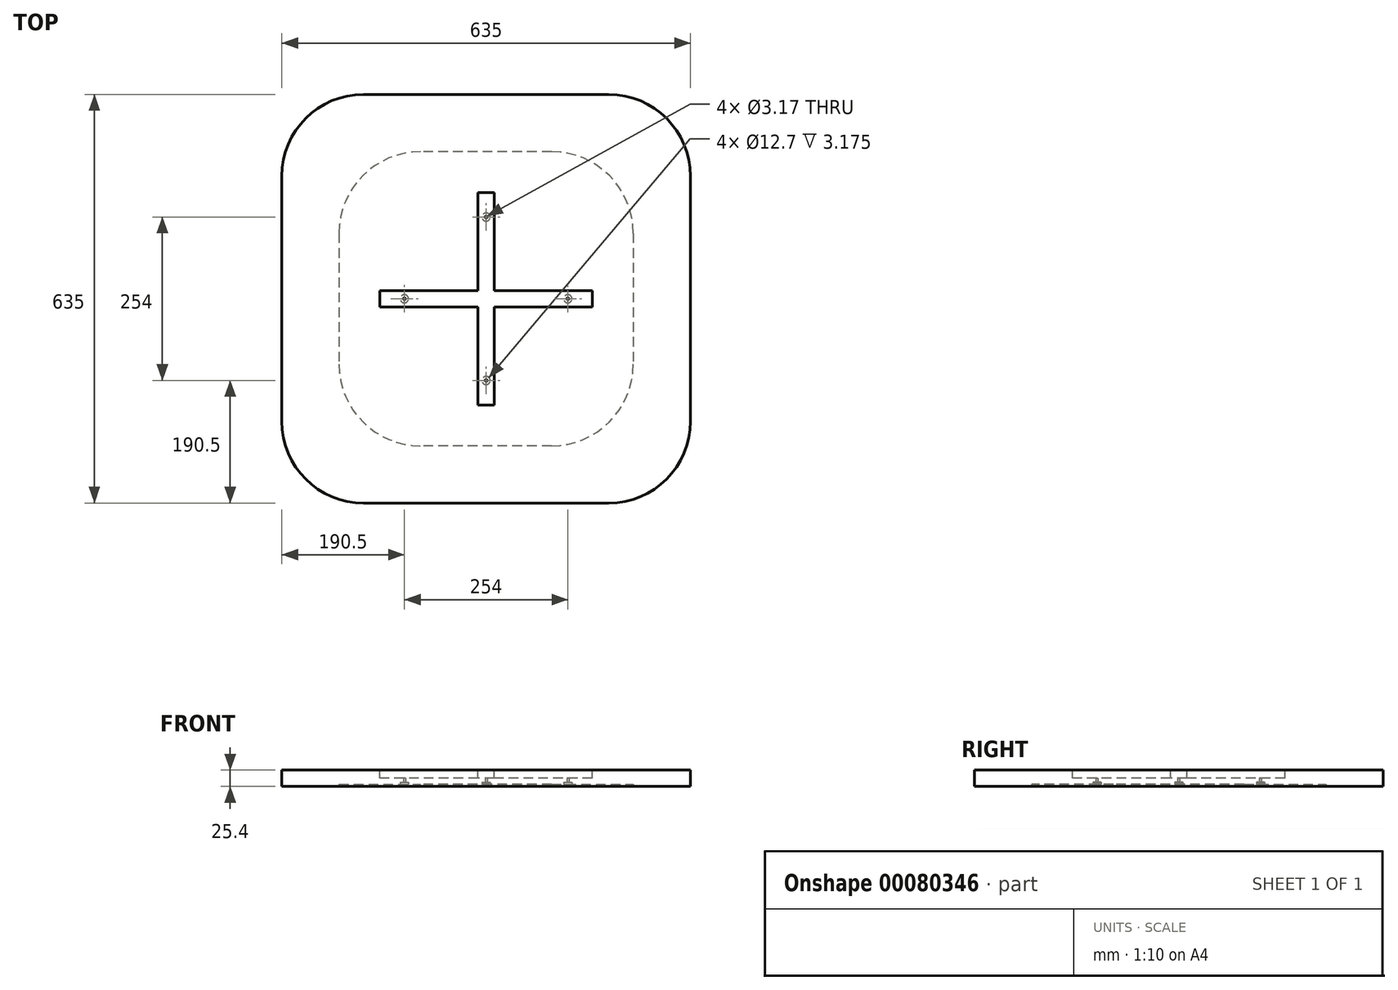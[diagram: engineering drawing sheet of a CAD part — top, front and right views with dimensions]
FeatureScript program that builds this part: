
annotation { "Feature Type Name" : "Feature", "Feature Type Description" : "" }
export const myFeature = defineFeature(function(context is Context, id is Id, definition is map)
    precondition{}
    {
        {
            var Q0;
            Q0=qCreatedBy(makeId("Top.planeOp"),FACE);
            var sketch = newSketch(context, id + "F0", { "sketchPlane" : qUnion([Q0])});
            skLineSegment(sketch, "E0.bottom", {"start": v(317.5, 317.5) * mm, "end": v(-317.5, 317.5) * mm});
            skLineSegment(sketch, "E0.top", {"start": v(317.5, -317.5) * mm, "end": v(-317.5, -317.5) * mm});
            skLineSegment(sketch, "E0.left", {"start": v(317.5, 317.5) * mm, "end": v(317.5, -317.5) * mm});
            skLineSegment(sketch, "E0.right", {"start": v(-317.5, 317.5) * mm, "end": v(-317.5, -317.5) * mm});
            skPoint(sketch, "E0.middle", {"position": v(0, 0) * mm});
            skSolve(sketch);
        }
        {
            var Q0;
            Q0=makeQuery(id+"F0.imprint","IMPRINT",FACE,{"disambiguationData":[TD([[makeQuery(id+"F0.imprint","IMPRINT",EDGE,{"derivedFrom":sQuery(id+"F0.wireOp",EDGE,"E0.bottom")}),1.0]])]});
            extrude(context, id + "F1", {"entities" : qUnion([Q0]), "depth" : 25.4 * mm});
        }
        {
            var Q0;
            Q0=makeQuery(id+"F1.opExtrude","CAP_FACE",FACE,{"disambiguationData":[OSD([sQuery(id+"F0.wireOp",EDGE,"E0.bottom"),sQuery(id+"F0.wireOp",EDGE,"E0.top"),sQuery(id+"F0.wireOp",EDGE,"E0.left"),sQuery(id+"F0.wireOp",EDGE,"E0.right")])],"isStart":false});
            var sketch = newSketch(context, id + "F8", { "sketchPlane" : qUnion([Q0])});
            skLineSegment(sketch, "E1.bottom", {"start": v(12.7, 165.1) * mm, "end": v(-12.7, 165.1) * mm});
            skLineSegment(sketch, "E1.top", {"start": v(12.7, -165.1) * mm, "end": v(-12.7, -165.1) * mm});
            skLineSegment(sketch, "E1.left", {"start": v(12.7, 165.1) * mm, "end": v(12.7, 12.7) * mm});
            skLineSegment(sketch, "E1.right", {"start": v(-12.7, 165.1) * mm, "end": v(-12.7, 12.7) * mm});
            skPoint(sketch, "E1.middle", {"position": v(0, 0) * mm});
            skLineSegment(sketch, "E2.bottom", {"start": v(165.1, 12.7) * mm, "end": v(12.7, 12.7) * mm});
            skLineSegment(sketch, "E2.top", {"start": v(165.1, -12.7) * mm, "end": v(12.7, -12.7) * mm});
            skLineSegment(sketch, "E2.left", {"start": v(165.1, 12.7) * mm, "end": v(165.1, -12.7) * mm});
            skLineSegment(sketch, "E2.right", {"start": v(-165.1, 12.7) * mm, "end": v(-165.1, -12.7) * mm});
            skLineSegment(sketch, "E3.trimOffspring", {"start": v(12.7, -12.7) * mm, "end": v(12.7, -165.1) * mm});
            skLineSegment(sketch, "E4.trimOffspring", {"start": v(-12.7, 12.7) * mm, "end": v(-165.1, 12.7) * mm});
            skLineSegment(sketch, "E5.trimOffspring", {"start": v(-12.7, -12.7) * mm, "end": v(-12.7, -165.1) * mm});
            skLineSegment(sketch, "E6.trimOffspring", {"start": v(-12.7, -12.7) * mm, "end": v(-165.1, -12.7) * mm});
            skSolve(sketch);
        }
        {
            var Q0;
            Q0=qSketchRegion(id+"F8",true);
            extrude(context, id + "F9", {"entities" : qUnion([Q0]), "operationType" : NewBodyOperationType.REMOVE, "oppositeDirection" : true, "depth" : 12.7 * mm});
        }
        {
            var Q0;
            Q0=makeQuery(id+"F1.opExtrude","SWEPT_EDGE",EDGE,{"disambiguationData":[OSD([sQuery(id+"F0.wireOp",EDGE,"E0.top"),sQuery(id+"F0.wireOp",EDGE,"E0.right")])]});
            var Q1;
            Q1=makeQuery(id+"F1.opExtrude","SWEPT_EDGE",EDGE,{"disambiguationData":[OSD([sQuery(id+"F0.wireOp",EDGE,"E0.top"),sQuery(id+"F0.wireOp",EDGE,"E0.left")])]});
            var Q2;
            Q2=makeQuery(id+"F1.opExtrude","SWEPT_EDGE",EDGE,{"disambiguationData":[OSD([sQuery(id+"F0.wireOp",EDGE,"E0.bottom"),sQuery(id+"F0.wireOp",EDGE,"E0.left")])]});
            var Q3;
            Q3=makeQuery(id+"F1.opExtrude","SWEPT_EDGE",EDGE,{"disambiguationData":[OSD([sQuery(id+"F0.wireOp",EDGE,"E0.bottom"),sQuery(id+"F0.wireOp",EDGE,"E0.right")])]});
            fillet(context, id + "F2", {"entities" : qUnion([Q0, Q1, Q2, Q3]), "radius" : 127 * mm, "tangentPropagation" : true, "allowEdgeOverflow" : false});
        }
        {
            var Q0;
            Q0=makeQuery(id+"F1.opExtrude","CAP_FACE",FACE,{"disambiguationData":[OSD([sQuery(id+"F0.wireOp",EDGE,"E0.bottom"),sQuery(id+"F0.wireOp",EDGE,"E0.top"),sQuery(id+"F0.wireOp",EDGE,"E0.left"),sQuery(id+"F0.wireOp",EDGE,"E0.right")])],"isStart":true});
            var sketch = newSketch(context, id + "F3", { "sketchPlane" : qUnion([Q0])});
            skLineSegment(sketch, "E7.bottom", {"start": v(228.6, -228.6) * mm, "end": v(-228.6, -228.6) * mm});
            skLineSegment(sketch, "E7.top", {"start": v(228.6, 228.6) * mm, "end": v(-228.6, 228.6) * mm});
            skLineSegment(sketch, "E7.left", {"start": v(228.6, -228.6) * mm, "end": v(228.6, 228.6) * mm});
            skLineSegment(sketch, "E7.right", {"start": v(-228.6, -228.6) * mm, "end": v(-228.6, 228.6) * mm});
            skPoint(sketch, "E7.middle", {"position": v(0, 0) * mm});
            skSolve(sketch);
        }
        {
            var Q0;
            Q0 = qSketchRegion(id + "F3", true);
            extrude(context, id + "F4", {"entities" : qUnion([Q0]), "operationType" : NewBodyOperationType.REMOVE, "oppositeDirection" : true, "depth" : 3.17 * mm});
        }
        {
            var Q0;
            Q0=makeQuery(id+"F4.boolean.opBoolean","COPY",EDGE,{"derivedFrom":makeQuery(id+"F4.opExtrude","SWEPT_EDGE",EDGE,{"disambiguationData":[OSD([sQuery(id+"F3.wireOp",EDGE,"E7.top"),sQuery(id+"F3.wireOp",EDGE,"E7.right")])]})});
            var Q1;
            Q1=makeQuery(id+"F4.boolean.opBoolean","COPY",EDGE,{"derivedFrom":makeQuery(id+"F4.opExtrude","SWEPT_EDGE",EDGE,{"disambiguationData":[OSD([sQuery(id+"F3.wireOp",EDGE,"E7.top"),sQuery(id+"F3.wireOp",EDGE,"E7.left")])]})});
            var Q2;
            Q2=makeQuery(id+"F4.boolean.opBoolean","COPY",EDGE,{"derivedFrom":makeQuery(id+"F4.opExtrude","SWEPT_EDGE",EDGE,{"disambiguationData":[OSD([sQuery(id+"F3.wireOp",EDGE,"E7.bottom"),sQuery(id+"F3.wireOp",EDGE,"E7.left")])]})});
            var Q3;
            Q3=makeQuery(id+"F4.boolean.opBoolean","COPY",EDGE,{"derivedFrom":makeQuery(id+"F4.opExtrude","SWEPT_EDGE",EDGE,{"disambiguationData":[OSD([sQuery(id+"F3.wireOp",EDGE,"E7.bottom"),sQuery(id+"F3.wireOp",EDGE,"E7.right")])]})});
            fillet(context, id + "F5", {"entities" : qUnion([Q0, Q1, Q2, Q3]), "radius" : 127 * mm, "tangentPropagation" : true, "allowEdgeOverflow" : false});
        }
        {
            var Q0;
            Q0=makeQuery(id+"F4.boolean.opBoolean","COPY",FACE,{"derivedFrom":makeQuery(id+"F4.opExtrude","CAP_FACE",FACE,{"disambiguationData":[OSD([sQuery(id+"F3.wireOp",EDGE,"E7.bottom"),sQuery(id+"F3.wireOp",EDGE,"E7.top"),sQuery(id+"F3.wireOp",EDGE,"E7.left"),sQuery(id+"F3.wireOp",EDGE,"E7.right")])],"isStart":false})});
            var sketch = newSketch(context, id + "F6", { "sketchPlane" : qUnion([Q0])});
            skPoint(sketch, "E8", {"position": v(-127, 0) * mm});
            skPoint(sketch, "E9", {"position": v(127, 0) * mm});
            skPoint(sketch, "E10", {"position": v(0, 127) * mm});
            skPoint(sketch, "E11", {"position": v(0, -127) * mm});
            skSolve(sketch);
        }
        {
            var Q0;
            Q0=sQuery(id+"F6.wireOp",VERTEX,"E8");
            var Q1;
            Q1=sQuery(id+"F6.wireOp",VERTEX,"E9");
            var Q2;
            Q2=sQuery(id+"F6.wireOp",VERTEX,"E10");
            var Q3;
            Q3=sQuery(id+"F6.wireOp",VERTEX,"E11");
            var Q4;
            Q4=makeQuery(id+"F1.opExtrude","SWEPT_BODY",BODY,{"disambiguationData":[OSD([sQuery(id+"F0.wireOp",EDGE,"E0.bottom"),sQuery(id+"F0.wireOp",EDGE,"E0.top"),sQuery(id+"F0.wireOp",EDGE,"E0.left"),sQuery(id+"F0.wireOp",EDGE,"E0.right")])]});
            hole(context, id + "F7", {"style" : HoleStyle.C_BORE, "endStyle" : HoleEndStyle.BLIND, "holeDiameter" : 3.17 * mm, "cBoreDiameter" : 12.7 * mm, "cBoreDepth" : 3.17 * mm, "holeDepth" : 63.5 * mm, "locations" : qUnion([Q0, Q1, Q2, Q3]), "scope" : qUnion([Q4])});
        }
    });
